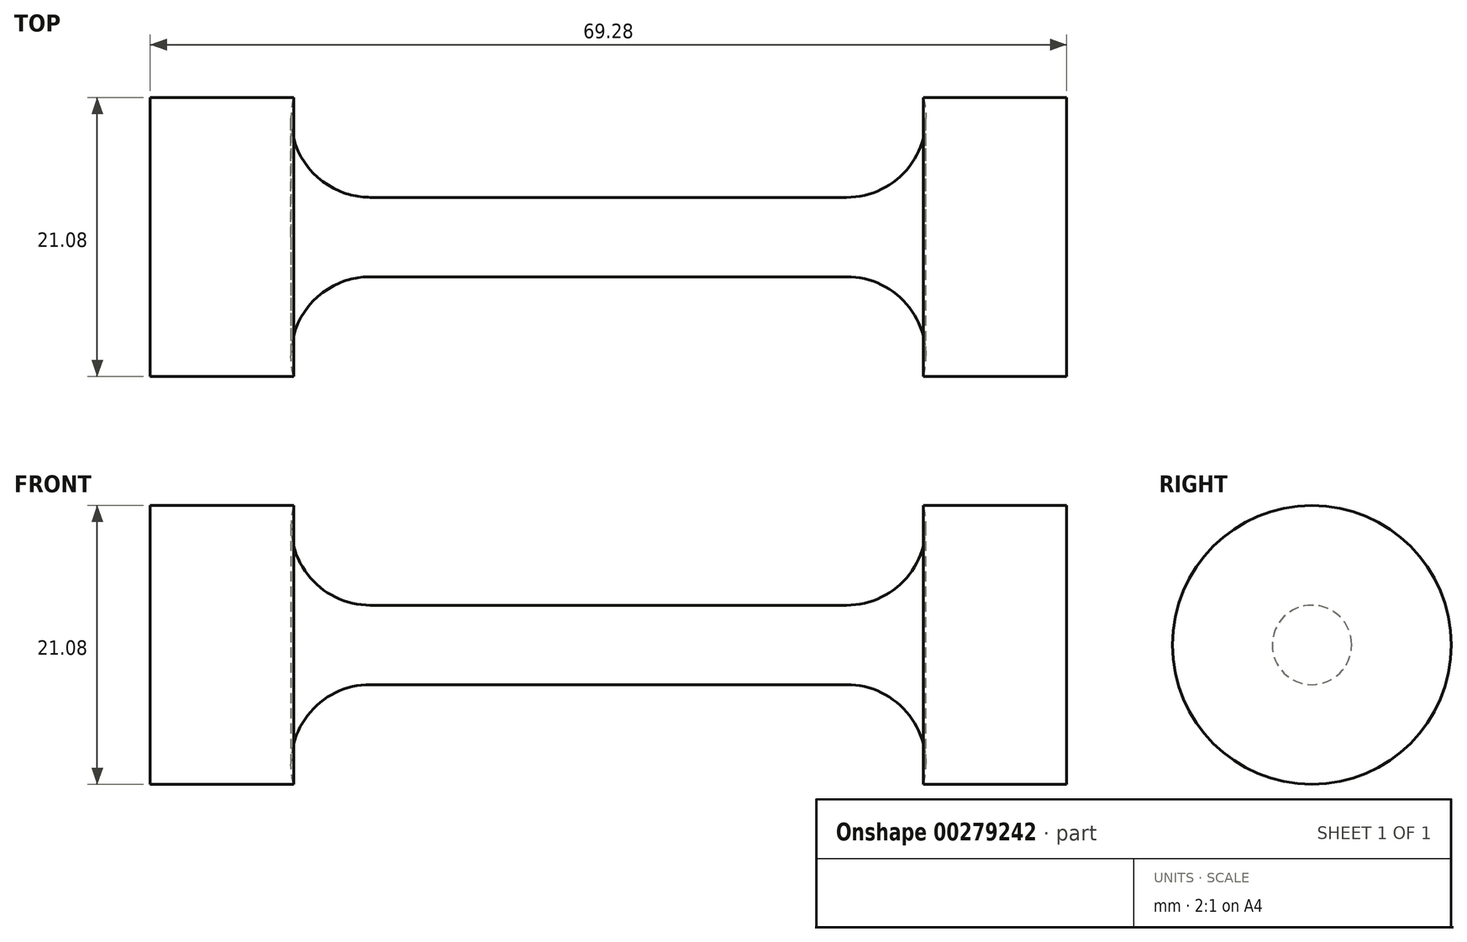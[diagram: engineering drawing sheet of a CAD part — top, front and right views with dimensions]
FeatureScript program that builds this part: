
annotation { "Feature Type Name" : "Feature", "Feature Type Description" : "" }
export const myFeature = defineFeature(function(context is Context, id is Id, definition is map)
    precondition{}
    {
        {
            var Q0;
            Q0=qCreatedBy(makeId("Front.planeOp"),FACE);
            var sketch = newSketch(context, id + "F0", { "sketchPlane" : qUnion([Q0])});
            skLineSegment(sketch, "E0", {"start": v(0, 3) * mm, "end": v(18, 3) * mm});
            skArc(sketch, "E1", {"start": v(18, 3) * mm, "mid": v(22.76, 5.34) * mm, "end": v(23.8, 10.54) * mm});
            skLineSegment(sketch, "E2", {"start": v(23.8, 10.54) * mm, "end": v(34.64, 10.54) * mm});
            skLineSegment(sketch, "E3", {"start": v(34.64, 10.54) * mm, "end": v(34.64, 0) * mm});
            skLineSegment(sketch, "E4.MirrorCS", {"start": v(0, 3) * mm, "end": v(-18, 3) * mm});
            skLineSegment(sketch, "E5.MirrorCS", {"start": v(-34.64, 10.54) * mm, "end": v(-34.64, 0) * mm});
            skLineSegment(sketch, "E6.MirrorCS", {"start": v(-23.8, 10.54) * mm, "end": v(-34.64, 10.54) * mm});
            skArc(sketch, "E7.MirrorCS", {"start": v(-18, 3) * mm, "mid": v(-22.76, 5.34) * mm, "end": v(-23.8, 10.54) * mm});
            skLineSegment(sketch, "E8", {"start": v(-34.64, 0) * mm, "end": v(34.64, 0) * mm});
            skSolve(sketch);
        }
        {
            var Q0;
            Q0=makeQuery(id+"F0.imprint","IMPRINT",FACE,{"disambiguationData":[TD([[makeQuery(id+"F0.imprint","IMPRINT",EDGE,{"derivedFrom":sQuery(id+"F0.wireOp",EDGE,"E0")}),-1.0]])]});
            var Q1;
            Q1=sQuery(id+"F0.wireOp",EDGE,"E8");
            revolve(context, id + "F1", {"entities" : qUnion([Q0]), "axis" : qUnion([Q1]), "revolveType" : RevolveType.FULL});
        }
    });
